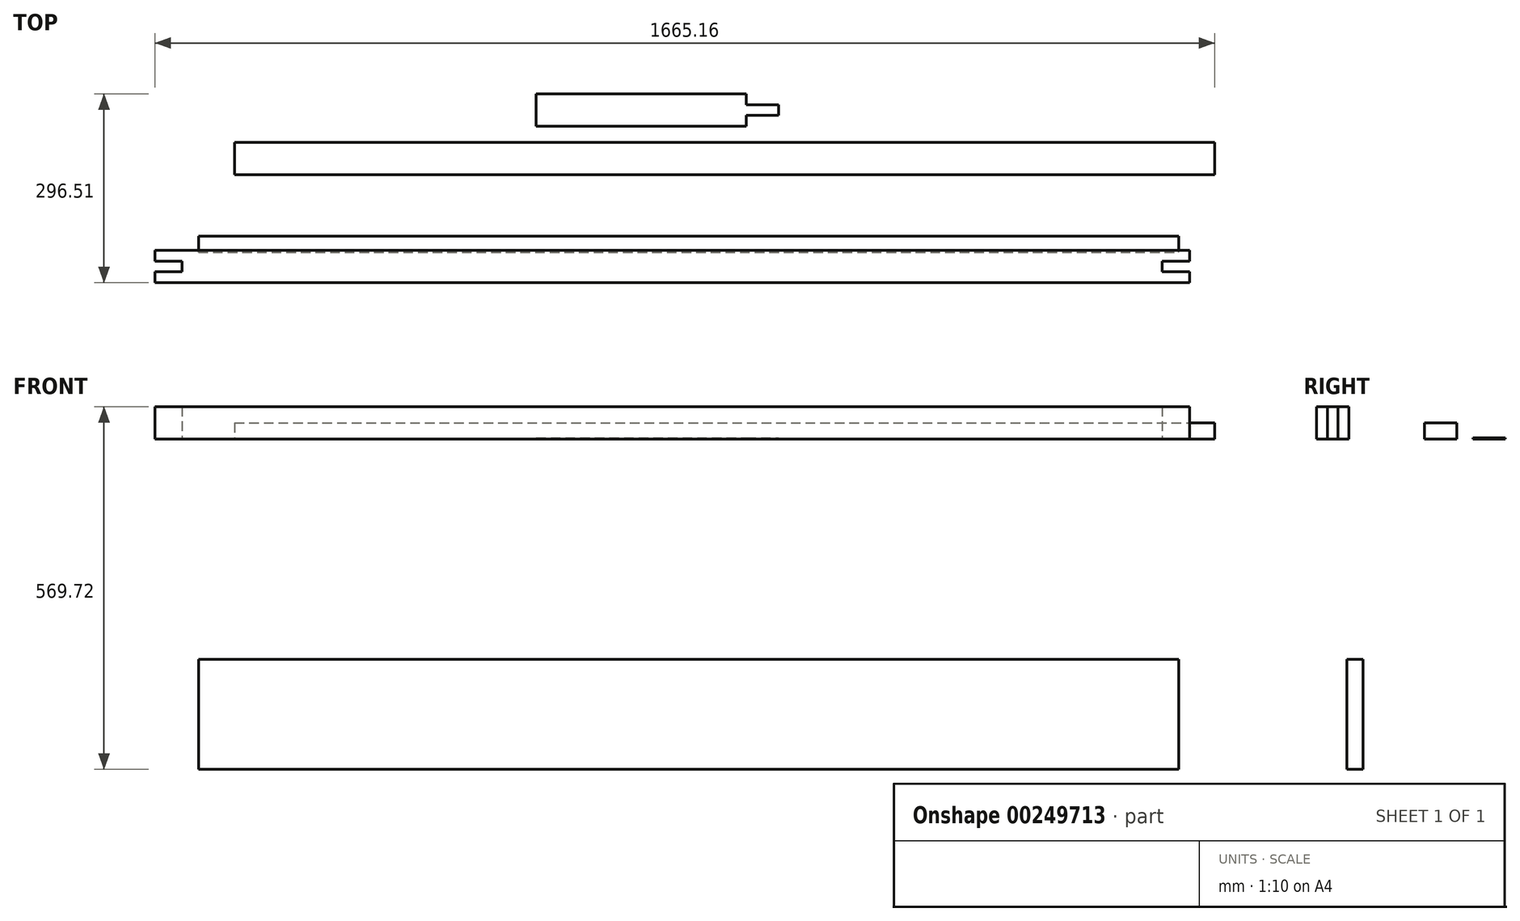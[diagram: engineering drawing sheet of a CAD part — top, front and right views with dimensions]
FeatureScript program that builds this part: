
annotation { "Feature Type Name" : "Feature", "Feature Type Description" : "" }
export const myFeature = defineFeature(function(context is Context, id is Id, definition is map)
    precondition{}
    {
        {
            var Q0;
            Q0=qCreatedBy(makeId("Top.planeOp"),FACE);
            var sketch = newSketch(context, id + "F0", { "sketchPlane" : qUnion([Q0])});
            skLineSegment(sketch, "E0", {"start": v(-811.94, -39.2) * mm, "end": v(-811.94, -22.26) * mm});
            skLineSegment(sketch, "E1", {"start": v(-811.94, -22.26) * mm, "end": v(813.66, -22.26) * mm});
            skLineSegment(sketch, "E2", {"start": v(813.66, -22.26) * mm, "end": v(813.66, -39.2) * mm});
            skLineSegment(sketch, "E3", {"start": v(813.66, -39.2) * mm, "end": v(770.8, -39.2) * mm});
            skLineSegment(sketch, "E4", {"start": v(770.8, -39.2) * mm, "end": v(770.8, -56.13) * mm});
            skLineSegment(sketch, "E5", {"start": v(770.8, -56.13) * mm, "end": v(813.66, -56.13) * mm});
            skLineSegment(sketch, "E6", {"start": v(813.66, -56.13) * mm, "end": v(813.66, -73.06) * mm});
            skLineSegment(sketch, "E7", {"start": v(813.66, -73.06) * mm, "end": v(-811.94, -73.06) * mm});
            skLineSegment(sketch, "E8", {"start": v(-811.94, -73.06) * mm, "end": v(-811.94, -56.13) * mm});
            skLineSegment(sketch, "E9", {"start": v(-811.94, -56.13) * mm, "end": v(-769.08, -56.13) * mm});
            skLineSegment(sketch, "E10", {"start": v(-769.08, -56.13) * mm, "end": v(-769.08, -39.2) * mm});
            skLineSegment(sketch, "E11", {"start": v(-769.08, -39.2) * mm, "end": v(-811.94, -39.2) * mm});
            skSolve(sketch);
        }
        {
            var Q0;
            Q0=makeQuery(id+"F0.imprint","IMPRINT",FACE,{"disambiguationData":[TD([[makeQuery(id+"F0.imprint","IMPRINT",EDGE,{"derivedFrom":sQuery(id+"F0.wireOp",EDGE,"E0")}),-1.0]])]});
            extrude(context, id + "F1", {"entities" : qUnion([Q0]), "depth" : 50.8 * mm});
        }
        {
            var Q0;
            Q0=qCreatedBy(makeId("Front.planeOp"),FACE);
            var sketch = newSketch(context, id + "F2", { "sketchPlane" : qUnion([Q0])});
            skLineSegment(sketch, "E12.bottom", {"start": v(-743.52, -345.88) * mm, "end": v(796.35, -345.88) * mm});
            skLineSegment(sketch, "E12.top", {"start": v(-743.52, -518.92) * mm, "end": v(796.35, -518.92) * mm});
            skLineSegment(sketch, "E12.left", {"start": v(-743.52, -345.88) * mm, "end": v(-743.52, -518.92) * mm});
            skLineSegment(sketch, "E12.right", {"start": v(796.35, -345.88) * mm, "end": v(796.35, -518.92) * mm});
            skSolve(sketch);
        }
        {
            var Q0;
            Q0=qSketchRegion(id+"F2",true);
            extrude(context, id + "F3", {"entities" : qUnion([Q0]), "depth" : 25.4 * mm});
        }
        {
            var Q0;
            Q0=qCreatedBy(makeId("Top.planeOp"),FACE);
            var sketch = newSketch(context, id + "F4", { "sketchPlane" : qUnion([Q0])});
            skLineSegment(sketch, "E13", {"start": v(-212.82, 223.45) * mm, "end": v(117.38, 223.45) * mm});
            skLineSegment(sketch, "E14", {"start": v(117.38, 206.52) * mm, "end": v(168.18, 206.52) * mm});
            skLineSegment(sketch, "E15", {"start": v(168.18, 206.52) * mm, "end": v(168.18, 189.59) * mm});
            skLineSegment(sketch, "E16", {"start": v(168.18, 189.59) * mm, "end": v(117.38, 189.59) * mm});
            skLineSegment(sketch, "E17", {"start": v(117.38, 189.59) * mm, "end": v(117.38, 172.65) * mm});
            skLineSegment(sketch, "E18", {"start": v(117.38, 172.65) * mm, "end": v(-212.82, 172.65) * mm});
            skLineSegment(sketch, "E19", {"start": v(-212.82, 172.65) * mm, "end": v(-212.82, 223.45) * mm});
            skLineSegment(sketch, "E20", {"start": v(117.38, 223.45) * mm, "end": v(117.38, 206.52) * mm});
            skSolve(sketch);
        }
        {
            var Q0;
            Q0=makeQuery(id+"F4.imprint","IMPRINT",FACE,{"disambiguationData":[TD([[makeQuery(id+"F4.imprint","IMPRINT",EDGE,{"derivedFrom":sQuery(id+"F4.wireOp",EDGE,"E13")}),-1.0]])]});
            extrude(context, id + "F5", {"entities" : qUnion([Q0]), "depth" : (1 + (11 / 16)) * mm});
        }
        {
            var Q0;
            Q0=qCreatedBy(makeId("Top.planeOp"),FACE);
            var sketch = newSketch(context, id + "F6", { "sketchPlane" : qUnion([Q0])});
            skLineSegment(sketch, "E21.bottom", {"start": v(-686.65, 147.06) * mm, "end": v(853.22, 147.06) * mm});
            skLineSegment(sketch, "E21.top", {"start": v(-686.65, 96.26) * mm, "end": v(853.22, 96.26) * mm});
            skLineSegment(sketch, "E21.left", {"start": v(-686.65, 147.06) * mm, "end": v(-686.65, 96.26) * mm});
            skLineSegment(sketch, "E21.right", {"start": v(853.22, 147.06) * mm, "end": v(853.22, 96.26) * mm});
            skSolve(sketch);
        }
        {
            var Q0;
            Q0=makeQuery(id+"F6.imprint","IMPRINT",FACE,{"disambiguationData":[TD([[makeQuery(id+"F6.imprint","IMPRINT",EDGE,{"derivedFrom":sQuery(id+"F6.wireOp",EDGE,"E21.bottom")}),-1.0]])]});
            extrude(context, id + "F7", {"entities" : qUnion([Q0]), "depth" : 25.4 * mm});
        }
    });
